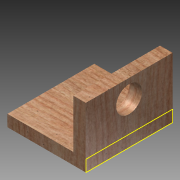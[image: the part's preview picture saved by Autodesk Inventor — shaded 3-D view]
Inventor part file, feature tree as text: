
AUTODESK INVENTOR PART (.ipt)
format: ipt  version: 2014 SP1 (Build 180222100, 222)  size: 121,344 bytes
history: native  units: in
note: dims shown in document units (in); Inventor stores cm internally (conversion verified against a paired STEP export)
features: sketch x4, extrude x3
ambient origin geometry x8: Origin, YZ Plane, XZ Plane, XY Plane, X Axis, Y Axis, Z Axis, Center Point
bodies: Solid1 (feature_tree)
feature tree (7):
  extrude  "Extrusion1"  Depth=5.96in
  sketch  "Sketch2"  dims[d2=0.794in d3=0.0in d4=0.859in]
  extrude  "Extrusion2"  Depth=0.859in
  extrude  "Extrusion3"  Depth=3.341in
  sketch  "Sketch1"  dims[d0=5.377in d1=5.96in]
  sketch  "Sketch3"  dims[d5=3.341in d6=0.0in d7=1.785in]
  sketch  "Sketch4"  dims[d8=1.2635in d9=3.341in d10=0.0in]
